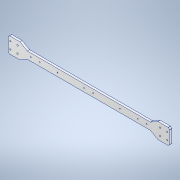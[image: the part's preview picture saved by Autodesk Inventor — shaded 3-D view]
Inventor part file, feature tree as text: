
AUTODESK INVENTOR PART (.ipt)
format: ipt  version: 2022 (Build 260153000, 153)  size: 132,608 bytes
history: imported  units: in
note: dims shown in document units (in); Inventor stores cm internally (conversion verified against a paired STEP export)
features: imported_body x1
ambient origin geometry x8: Origin, YZ Plane, XZ Plane, XY Plane, X Axis, Y Axis, Z Axis, Center Point
bodies: Solid1 (imported_parasolid), Body1 (imported_parasolid)
feature tree (1):
  imported_body  NMx_Import_Brep_tag  [imported B-rep: ~42 faces, bbox_mm=[453.0, 44.0, 6.35]]
